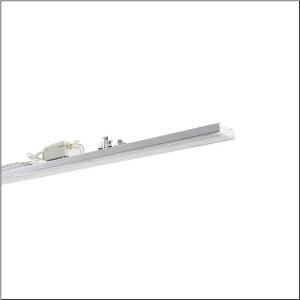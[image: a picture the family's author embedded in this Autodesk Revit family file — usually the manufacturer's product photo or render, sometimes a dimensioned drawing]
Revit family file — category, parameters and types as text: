
# Revit family: licross_r__21_recessed_mo_52tl117n485g_e718
name_source: partatom
category: Lighting Fixtures
units: mm (PartAtom-declared; Revit-internal decimal feet)

## family parameters
Cut with Voids When Loaded = No
Host = Face
Light Source = No
Part Type = Normal
Room Calculation Point = No
Round Connector Dimension = Use Diameter
Shared = No

## types (1)
- Licross® 21 Recessed MO (1 x LED, 8680 lm, 47.9 W, 4000K)
    Apparent Load = 48 VA
    CIE Flux Codes = 89 96 99 100 100
    Color Rendering = 80
    Color Temperature = 4000K
    Default Elevation = 1800 mm
    Description = Licross® 21 Recessed MO, luminaire insert, of sheet steel, galvanised, coil coated, white, length: 1.500mm, width: 66mm, height: 67mm, LED rated luminous flux: 8.680lm, light colour: 840, control gear: ON/OFF, with plug, 3-pole, with phase selection, mains connection: 220..240V, AC, 50/60Hz, rated input power: 48W, halogen-free wiring, primary light control with lens, of plastic, primary optical cover: cover, of PMMA, light emission: direct distribution, primary light characteristic: symmetric, protection rating (complete): IP40, insulation class (complete): insulation class I (protective earthing), certification: CE, ENEC, VDE, UKCA, protection symbol: D if used in an environment without relevant dust loads with corresponding accessories, impact resistance: IK06, permissible ambient temperature for indoor applications: -35..+40°C, corresponds to IFS (International Featured Standards) requirements for safety and quality in the food industry, reducing of maximum allowable ambient temperature of 5°C with ceiling mounting, LABS conformity tested according to VDMA 24364:2018-05, packaging unit: 1 piece
    Height = 58 mm
    Lamp = 1 x LED
    Lamp Light Flux = 8680 lm
    Lamp Power = 47.9 W
    Lamp count = 1
    Length = 1500 mm
    Luminous efficacy = 181 lm/W
    Manufacturer = Siteco
    ModVariant = No
    Model = 52TL117N485G
    Mounting Place = Ceiling
    Mounting Type = Pendant
    Number of Poles = 1
    OnlyDefault = Yes
    Power Factor = 1
    Product Name = Licross® 21 Recessed MO
    Product group = luminaire insert
    ProductGroupID = 901
    Protection Class = Protection class I
    Protection Degree = IP 40
    RLX_Detail_Level = 1
    RLX_Emergency_Light_Flux = 0 lm
    RLX_Emergency_Type = 0
    RLX_Emergency_Type_DB = No
    RlxData = <blob elided: 20853 chars, md5=b4c8f59c>
    Socket = socket
    Standby Power = 0 W
    System Light Flux = 8680 lm
    System Power = 48 W
    Type Comments = Product without accessories
    Type Image = l_1296930.jpg
    URL = http://relux.com
    VarID = ---
    Voltage = 0 V
    Weight = 0.00 kg
    Width = 66 mm

## geometry (parser evidence)
native form markers: Blend x4, Sweep x11
no freeform markers — native parametric forms only
